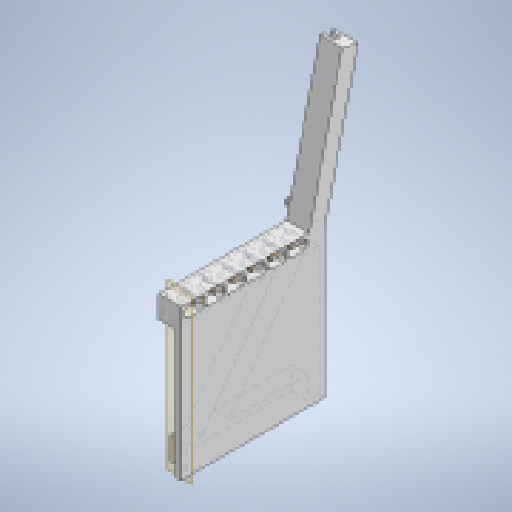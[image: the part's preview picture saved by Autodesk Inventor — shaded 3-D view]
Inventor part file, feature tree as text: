
AUTODESK INVENTOR PART (.ipt)
format: ipt  version: 2023 (Build 270158030, 158C)  size: 413,696 bytes
history: native  units: mm
features: extrude x7, sketch x7, reference x5, other x5, plane x1, pattern_linear x1, fillet x1, projected_geometry x1
ambient origin geometry x8: Origin, YZ Plane, XZ Plane, XY Plane, X Axis, Y Axis, Z Axis, Center Point
bodies: Solid1 (feature_tree)
feature tree (28):
  extrude  "Extrusion1"  Depth=70.0mm
  extrude  "Extrusion2"  Depth=70.0mm
  extrude  "Extrusion3"  Depth=400.0mm
  extrude  "Extrusion4"  [1 undecoded]
  plane  "Work Plane1"
  extrude  "Extrusion5"  Depth=450.0mm
  pattern_linear  "Rectangular Pattern1"  Count1=7 Spacing1=0.0mm
  extrude  "Extrusion6"  Depth=60.0mm
  fillet  "Fillet1"  Radius=30.0mm
  extrude  "Extrusion7"  Depth=10.0mm
  sketch  "Sketch1"  dims[d0=380.0mm d1=70.0mm]
  sketch  "Sketch2"  dims[d2=190.0mm d3=70.0mm]
  sketch  "Sketch3"  dims[d4=50.0mm d5=400.0mm]
  sketch  "Sketch4"  dims[d6=9.599311mm d7=-13.477291mm]
  projected_geometry  "Projected Loop1"
  sketch  "Sketch6"  dims[d8=70.0mm d9=450.0mm]
  reference  "Reference5"
  reference  "Reference6"
  reference  "Reference7"
  reference  "Reference8"
  reference  "Reference9"
  other  "hinges"
  sketch  "Sketch7"  dims[d10=35.0mm]
  other  "locating-pin"
  sketch  "Sketch8"  dims[d11=35.0mm d12=70.0mm d13=0.0mm d14=60.0mm d15=30.0mm d16=10.0mm d17=10.0mm d18=10.0mm d19=60.0mm d21=65.0mm d22=10.0mm d24=10.0mm d26=0.0mm d27=0.0mm d28=17.976891mm d29=50.0mm d30=50.0mm d31=450.0mm d32=450.0mm d33=10.0mm d34=0.0mm d35=20.0mm d36=0.0mm d37=-30.0mm d40=0.5mm d41=9.0mm d42=14.0mm d43=8.5mm d44=30.0mm d45=0.0mm d46=60.0mm d48=60.0mm d49=20.0mm d50=24.0mm d51=22.0mm d52=30.0mm d53=0.0mm d54=4.0mm d55=22.0mm d56=14.0mm d57=14.0mm d58=100.0mm d59=10.0mm d60=30.0mm d61=0.0mm]
  other  "<userpath>\Documents\0004-inventor\3D-CAD-main\primary-engineer-bench.iam"
  other  "primary-engineer-bench.iam"
  other  "flip-up-side:1"
note: 1 required parameter value undecoded (feature->parameter linkage not recoverable at this tier; creation-order binding heuristic only, values carry confidence <= 0.55)
